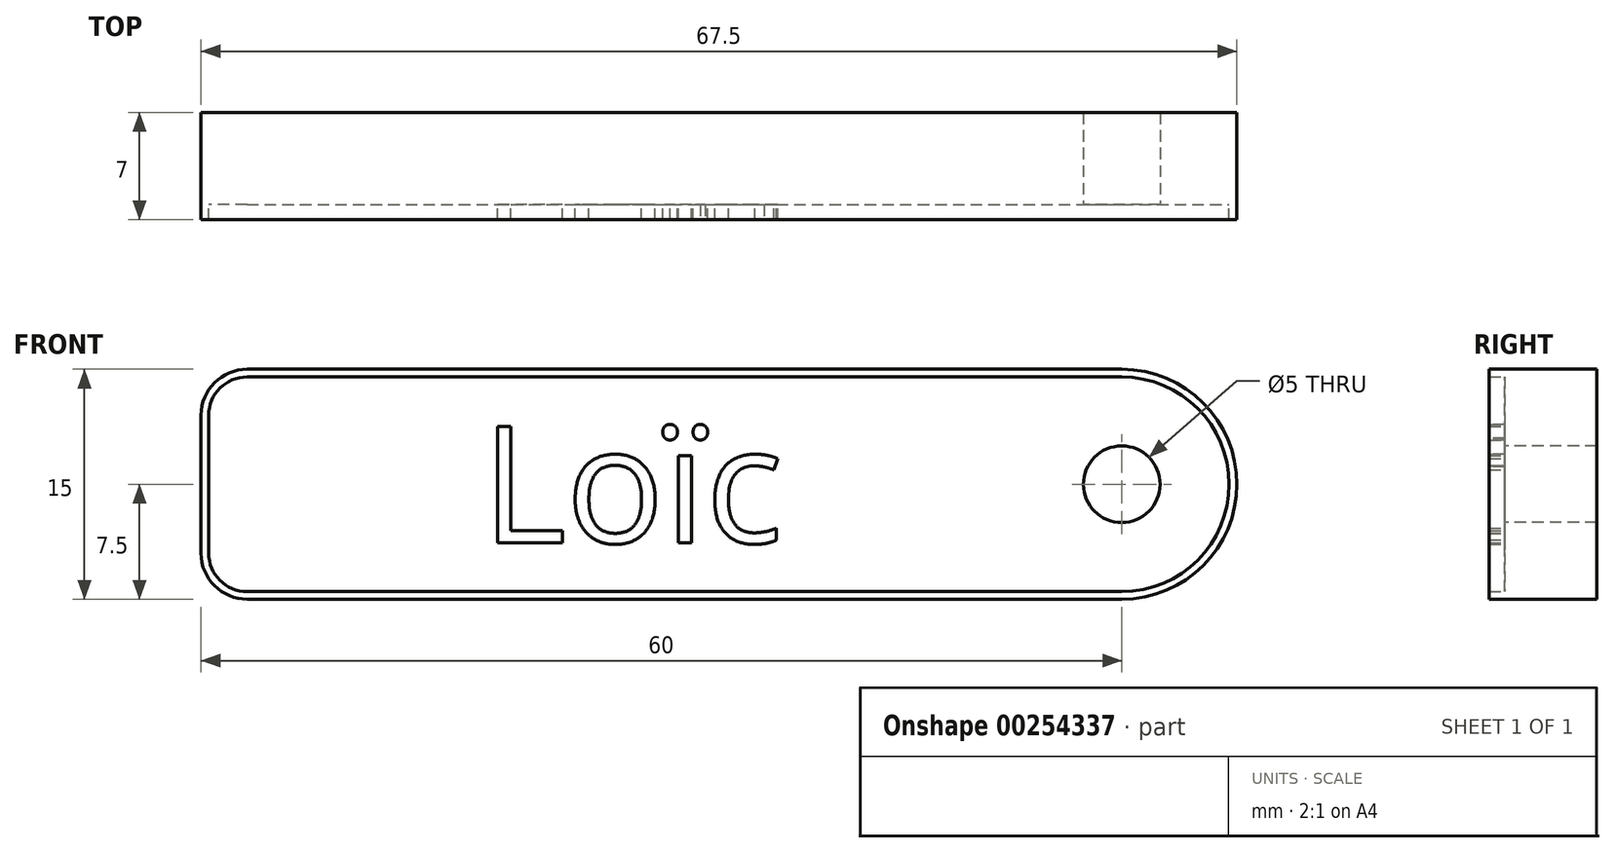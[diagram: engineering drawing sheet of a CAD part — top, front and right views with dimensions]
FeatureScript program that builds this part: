
annotation { "Feature Type Name" : "Feature", "Feature Type Description" : "" }
export const myFeature = defineFeature(function(context is Context, id is Id, definition is map)
    precondition{}
    {
        {
            var Q0;
            Q0=qCreatedBy(makeId("Front.planeOp"),FACE);
            var sketch = newSketch(context, id + "F0", { "sketchPlane" : qUnion([Q0])});
            skLineSegment(sketch, "E0.bottom", {"start": v(3, 7.5) * mm, "end": v(60, 7.5) * mm});
            skLineSegment(sketch, "E0.top", {"start": v(3, -7.5) * mm, "end": v(60, -7.5) * mm});
            skLineSegment(sketch, "E0.left", {"start": v(0, 4.5) * mm, "end": v(0, -4.5) * mm});
            skArc(sketch, "E1", {"start": v(60, -7.5) * mm, "mid": v(67.5, 0) * mm, "end": v(60, 7.5) * mm});
            skCircle(sketch, "E2", {"center": v(60, 0) * mm, "radius": 2.5 * mm});
            skPoint(sketch, "E3.visualSharp", {"position": v(0, 7.5) * mm});
            skArc(sketch, "E3.filletArc", {"start": v(3, 7.5) * mm, "mid": v(0.88, 6.62) * mm, "end": v(0, 4.5) * mm});
            skPoint(sketch, "E4.visualSharp", {"position": v(0, -7.5) * mm});
            skArc(sketch, "E4.filletArc", {"start": v(0, -4.5) * mm, "mid": v(0.88, -6.62) * mm, "end": v(3, -7.5) * mm});
            skSolve(sketch);
        }
        {
            var Q0;
            Q0 = qSketchRegion(id + "F0", true);
            extrude(context, id + "F1", {"entities" : qUnion([Q0]), "oppositeDirection" : true, "depth" : 3 * mm});
        }
        {
            var Q0;
            Q0=makeQuery(id+"F1.opExtrude","CAP_FACE",FACE,{"disambiguationData":[OSD([sQuery(id+"F0.wireOp",EDGE,"E0.bottom"),sQuery(id+"F0.wireOp",EDGE,"E0.top"),sQuery(id+"F0.wireOp",EDGE,"E0.left"),sQuery(id+"F0.wireOp",EDGE,"E1"),sQuery(id+"F0.wireOp",EDGE,"E2"),sQuery(id+"F0.wireOp",EDGE,"E3.filletArc"),sQuery(id+"F0.wireOp",EDGE,"E4.filletArc")])],"isStart":true});
            extrude(context, id + "F2", {"entities" : qUnion([Q0]), "operationType" : NewBodyOperationType.ADD, "depth" : 3 * mm});
        }
        {
            var Q0;
            Q0=makeQuery(id+"F2.opExtrude","CAP_FACE",FACE,{"disambiguationData":[OSD([sQuery(id+"F0.wireOp",EDGE,"E0.bottom"),sQuery(id+"F0.wireOp",EDGE,"E0.top"),sQuery(id+"F0.wireOp",EDGE,"E0.left"),sQuery(id+"F0.wireOp",EDGE,"E1"),sQuery(id+"F0.wireOp",EDGE,"E2"),sQuery(id+"F0.wireOp",EDGE,"E3.filletArc"),sQuery(id+"F0.wireOp",EDGE,"E4.filletArc")])],"isStart":false});
            var sketch = newSketch(context, id + "F3", { "sketchPlane" : qUnion([Q0])});
            skText(sketch, "E5", { "text": "Loïc", "fontName": "OpenSans-Regular.ttf"});
            skPoint(sketch, "E5.firstSnap0", {"position": v(67.5, -3.82) * mm});
            const initialGuessF3  = {"E5": [0.01828, -0.00382, 1, 0, 0.00764]};
            skSetInitialGuess(sketch, initialGuessF3);
            skSolve(sketch);
        }
        {
            var Q0;
            Q0 = qSketchRegion(id + "F3", true);
            extrude(context, id + "F4", {"entities" : qUnion([Q0]), "operationType" : NewBodyOperationType.ADD, "depth" : 1 * mm});
        }
        {
            var Q0;
            {var subQ0=sQuery(id+"F0.wireOp",EDGE,"E0.bottom");var subQ1=sQuery(id+"F0.wireOp",EDGE,"E4.filletArc");var subQ2=sQuery(id+"F0.wireOp",EDGE,"E3.filletArc");var subQ3=sQuery(id+"F0.wireOp",EDGE,"E0.left");var subQ4=sQuery(id+"F0.wireOp",EDGE,"E1");var subQ5=sQuery(id+"F0.wireOp",EDGE,"E0.top");var subQ6=sQuery(id+"F0.wireOp",EDGE,"E2");Q0=makeQuery(id+"F4.boolean.opBoolean","SPLIT",FACE,{"disambiguationData":[TD([makeQuery(id+"F1.opExtrude","SWEPT_FACE",FACE,{"disambiguationData":[OSD([subQ0])]})])],"derivedFrom":makeQuery(id+"F2.opExtrude","CAP_FACE",FACE,{"disambiguationData":[OSD([subQ0,subQ5,subQ3,subQ4,subQ6,subQ2,subQ1])],"isStart":false})});}
            var sketch = newSketch(context, id + "F5", { "sketchPlane" : qUnion([Q0])});
            skArc(sketch, "E6.0", {"start": v(3, 7) * mm, "mid": v(1.23, 6.27) * mm, "end": v(0.5, 4.5) * mm});
            skArc(sketch, "E6.1", {"start": v(60, -7) * mm, "mid": v(67, 0) * mm, "end": v(60, 7) * mm});
            skLineSegment(sketch, "E6.2", {"start": v(3, -7) * mm, "end": v(60, -7) * mm});
            skLineSegment(sketch, "E6.3", {"start": v(3, 7) * mm, "end": v(60, 7) * mm});
            skArc(sketch, "E6.4", {"start": v(0.5, -4.5) * mm, "mid": v(1.23, -6.27) * mm, "end": v(3, -7) * mm});
            skLineSegment(sketch, "E6.5", {"start": v(0.5, 4.5) * mm, "end": v(0.5, -4.5) * mm});
            skSolve(sketch);
        }
        {
            var Q0;
            Q0=makeQuery(id+"F5.imprint","IMPRINT",FACE,{"disambiguationData":[TD([[makeQuery(id+"F5.imprint","IMPRINT",EDGE,{"derivedFrom":sQuery(id+"F5.wireOp",EDGE,"E6.0")}),-1.0]])]});
            extrude(context, id + "F6", {"entities" : qUnion([Q0]), "operationType" : NewBodyOperationType.ADD, "depth" : 1 * mm});
        }
    });
